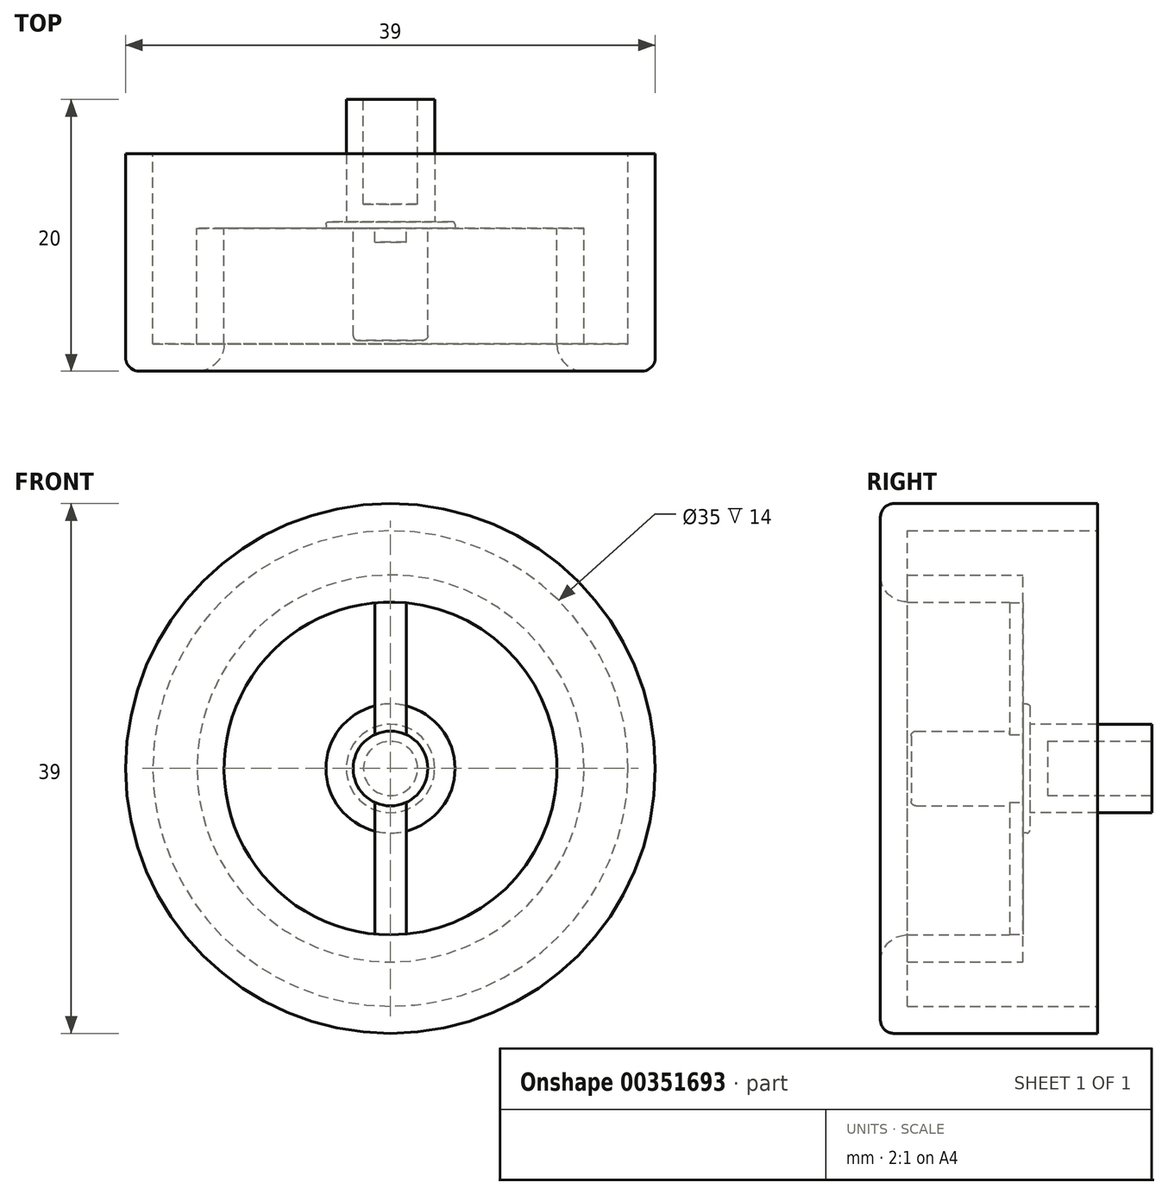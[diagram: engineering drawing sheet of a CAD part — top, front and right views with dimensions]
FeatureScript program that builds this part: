
annotation { "Feature Type Name" : "Feature", "Feature Type Description" : "" }
export const myFeature = defineFeature(function(context is Context, id is Id, definition is map)
    precondition{}
    {
        {
            var Q0;
            Q0=qCreatedBy(makeId("Front.planeOp"),FACE);
            var sketch = newSketch(context, id + "F0", { "sketchPlane" : qUnion([Q0])});
            skCircle(sketch, "E0", {"center": v(0, 0) * mm, "radius": 19.5 * mm});
            skCircle(sketch, "E1", {"center": v(0, 0) * mm, "radius": 12.25 * mm});
            skSolve(sketch);
        }
        {
            var Q0;
            Q0=makeQuery(id+"F0.imprint","IMPRINT",FACE,{"disambiguationData":[TD([[makeQuery(id+"F0.imprint","IMPRINT",EDGE,{"derivedFrom":sQuery(id+"F0.wireOp",EDGE,"E0")}),1.0]])]});
            extrude(context, id + "F1", {"entities" : qUnion([Q0]), "endBound" : BoundingType.SYMMETRIC, "depth" : 16 * mm});
        }
        {
            var Q0;
            Q0=makeQuery(id+"F1.opExtrude","CAP_FACE",FACE,{"disambiguationData":[OSD([sQuery(id+"F0.wireOp",EDGE,"E0"),sQuery(id+"F0.wireOp",EDGE,"E1")])],"isStart":true});
            shell(context, id + "F2", {"entities" : qUnion([Q0]), "thickness" : 2 * mm});
        }
        {
            var Q0;
            {var subQ0=sQuery(id+"F0.wireOp",EDGE,"E1");var subQ1=sQuery(id+"F0.wireOp",EDGE,"E0");Q0=makeQuery(id+"F2.opShell","OFFSET_FACE",FACE,{"disambiguationData":[OSD([subQ1,subQ0]),TDD([makeQuery(id+"F1.opExtrude","CAP_FACE",FACE,{"disambiguationData":[OSD([subQ1,subQ0])],"isStart":true})])]});}
            extrude(context, id + "F3", {"entities" : qUnion([Q0]), "operationType" : NewBodyOperationType.REMOVE, "oppositeDirection" : true, "depth" : 5.5 * mm});
        }
        {
            var Q0;
            Q0=makeQuery(id+"F3.boolean.opBoolean","COPY",FACE,{"derivedFrom":makeQuery(id+"F3.opExtrude","CAP_FACE",FACE,{"disambiguationData":[OSD([sQuery(id+"F0.wireOp",EDGE,"E0"),sQuery(id+"F0.wireOp",EDGE,"E1")])],"isStart":false})});
            cPlane(context, id + "F4", {"entities" : qUnion([Q0]), "cplaneType" : CPlaneType.OFFSET, "offset" : 0 * mm, "width" : 152.4 * mm, "height" : 152.4 * mm});
        }
        {
            var Q0;
            Q0=qCreatedBy(id+"F4.planeOp",FACE);
            var sketch = newSketch(context, id + "F5", { "sketchPlane" : qUnion([Q0])});
            skCircle(sketch, "E2", {"center": v(0, 0) * mm, "radius": 4.75 * mm});
            skSolve(sketch);
        }
        {
            var Q0;
            Q0=qCreatedBy(id+"F4.planeOp",FACE);
            var sketch = newSketch(context, id + "F6", { "sketchPlane" : qUnion([Q0])});
            skLineSegment(sketch, "E3.bottom", {"start": v(-1.16, 12.25) * mm, "end": v(1.16, 12.25) * mm});
            skLineSegment(sketch, "E3.top", {"start": v(-1.16, -12.25) * mm, "end": v(1.16, -12.25) * mm});
            skLineSegment(sketch, "E3.left", {"start": v(-1.16, 12.25) * mm, "end": v(-1.16, -12.25) * mm});
            skLineSegment(sketch, "E3.right", {"start": v(1.16, 12.25) * mm, "end": v(1.16, -12.25) * mm});
            skPoint(sketch, "E3.middle", {"position": v(0, 0) * mm});
            skSolve(sketch);
        }
        {
            var Q0;
            Q0=makeQuery(id+"F2iAADW7qtTHpJc_1.2.F6.imprint","IMPRINT",FACE,{"disambiguationData":[TD([[makeQuery(id+"F2iAADW7qtTHpJc_1.2.F6.imprint","IMPRINT",EDGE,{"derivedFrom":sQuery(id+"F2iAADW7qtTHpJc_1.2.F6.wireOp",EDGE,"E3.bottom")}),-1.0]])]});
            var Q1;
            Q1=makeQuery(id+"F6.imprint","IMPRINT",FACE,{"disambiguationData":[TD([[makeQuery(id+"F6.imprint","IMPRINT",EDGE,{"derivedFrom":sQuery(id+"F6.wireOp",EDGE,"E3.bottom")}),-1.0]])]});
            var Q2;
            Q2=makeQuery(id+"F2iAADW7qtTHpJc_1.1.F6.imprint","IMPRINT",FACE,{"disambiguationData":[TD([[makeQuery(id+"F2iAADW7qtTHpJc_1.1.F6.imprint","IMPRINT",EDGE,{"derivedFrom":sQuery(id+"F2iAADW7qtTHpJc_1.1.F6.wireOp",EDGE,"E3.bottom")}),-1.0]])]});
            extrude(context, id + "F7", {"entities" : qUnion([Q0, Q1, Q2]), "operationType" : NewBodyOperationType.ADD, "oppositeDirection" : true, "depth" : 1 * mm});
        }
        {
            var Q0;
            Q0 = qSketchRegion(id + "F5", true);
            extrude(context, id + "F8", {"entities" : qUnion([Q0]), "operationType" : NewBodyOperationType.ADD, "depth" : 0.5 * mm});
        }
        {
            var Q0;
            Q0=makeQuery(id+"F8.opExtrude","CAP_EDGE",EDGE,{"disambiguationData":[OSD([sQuery(id+"F5.wireOp",EDGE,"E2")])],"isStart":false});
            fillet(context, id + "F9", {"entities" : qUnion([Q0]), "radius" : 0.2 * mm, "tangentPropagation" : true, "allowEdgeOverflow" : false});
        }
        {
            var Q0;
            Q0=makeQuery(id+"F8.opExtrude","CAP_FACE",FACE,{"disambiguationData":[OSD([sQuery(id+"F5.wireOp",EDGE,"E2")])],"isStart":false});
            var sketch = newSketch(context, id + "F10", { "sketchPlane" : qUnion([Q0])});
            skCircle(sketch, "E4", {"center": v(0, 0) * mm, "radius": 3.25 * mm});
            skSolve(sketch);
        }
        {
            var Q0;
            Q0 = qSketchRegion(id + "F10", true);
            extrude(context, id + "F11", {"entities" : qUnion([Q0]), "operationType" : NewBodyOperationType.ADD, "depth" : 9 * mm});
        }
        {
            var Q0;
            Q0=makeQuery(id+"F11.opExtrude","CAP_FACE",FACE,{"disambiguationData":[OSD([sQuery(id+"F10.wireOp",EDGE,"E4")])],"isStart":false});
            var sketch = newSketch(context, id + "F12", { "sketchPlane" : qUnion([Q0])});
            skCircle(sketch, "E5", {"center": v(0, 0) * mm, "radius": 2 * mm});
            skSolve(sketch);
        }
        {
            var Q0;
            Q0=makeQuery(id+"F12.imprint","IMPRINT",FACE,{"disambiguationData":[TD([[makeQuery(id+"F12.imprint","IMPRINT",EDGE,{"derivedFrom":sQuery(id+"F12.wireOp",EDGE,"E5")}),1.0]])]});
            extrude(context, id + "F13", {"entities" : qUnion([Q0]), "operationType" : NewBodyOperationType.REMOVE, "oppositeDirection" : true, "depth" : 7.7 * mm});
        }
        {
            var Q0;
            Q0=makeQuery(id+"F1.opExtrude","CAP_EDGE",EDGE,{"disambiguationData":[OSD([sQuery(id+"F0.wireOp",EDGE,"E0")])],"isStart":false});
            fillet(context, id + "F14", {"entities" : qUnion([Q0]), "radius" : 1 * mm, "tangentPropagation" : true, "allowEdgeOverflow" : false});
        }
        {
            var Q0;
            Q0=makeQuery(id+"F1.opExtrude","CAP_EDGE",EDGE,{"disambiguationData":[OSD([sQuery(id+"F0.wireOp",EDGE,"E1")])],"isStart":false});
            fillet(context, id + "F15", {"entities" : qUnion([Q0]), "radius" : 2 * mm, "tangentPropagation" : true, "allowEdgeOverflow" : false});
        }
        {
            var Q0;
            Q0=qCreatedBy(id+"F4.planeOp",FACE);
            var sketch = newSketch(context, id + "F16", { "sketchPlane" : qUnion([Q0])});
            skCircle(sketch, "E6", {"center": v(0, 0) * mm, "radius": 2.75 * mm});
            skSolve(sketch);
        }
        {
            var Q0;
            Q0 = qSketchRegion(id + "F16", true);
            extrude(context, id + "F17", {"entities" : qUnion([Q0]), "operationType" : NewBodyOperationType.ADD, "oppositeDirection" : true, "depth" : 8.23 * mm});
        }
        {
            var Q0;
            Q0=makeQuery(id+"F17.opExtrude","CAP_EDGE",EDGE,{"disambiguationData":[OSD([sQuery(id+"F16.wireOp",EDGE,"E6")])],"isStart":false});
            fillet(context, id + "F18", {"entities" : qUnion([Q0]), "radius" : 0.35 * mm, "tangentPropagation" : true, "allowEdgeOverflow" : false});
        }
    });
